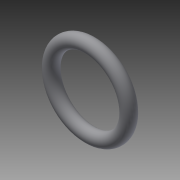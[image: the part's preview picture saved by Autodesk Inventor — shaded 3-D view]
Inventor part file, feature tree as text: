
AUTODESK INVENTOR PART (.ipt)
format: ipt  version: 2014 SP1 (Build 180222100, 222)  size: 115,200 bytes
history: native  units: in
note: dims shown in document units (in); Inventor stores cm internally (conversion verified against a paired STEP export)
features: revolve x1, sketch x1
ambient origin geometry x8: Origin, YZ Plane, XZ Plane, XY Plane, X Axis, Y Axis, Z Axis, Center Point
bodies: Solid1 (feature_tree)
feature tree (2):
  revolve  "Revolution1"  [1 undecoded]
  sketch  "Sketch1"  dims[d0=0.06in d1=0.175in d2=90.0deg]
note: 1 required parameter value undecoded (feature->parameter linkage not recoverable at this tier; creation-order binding heuristic only, values carry confidence <= 0.55)
